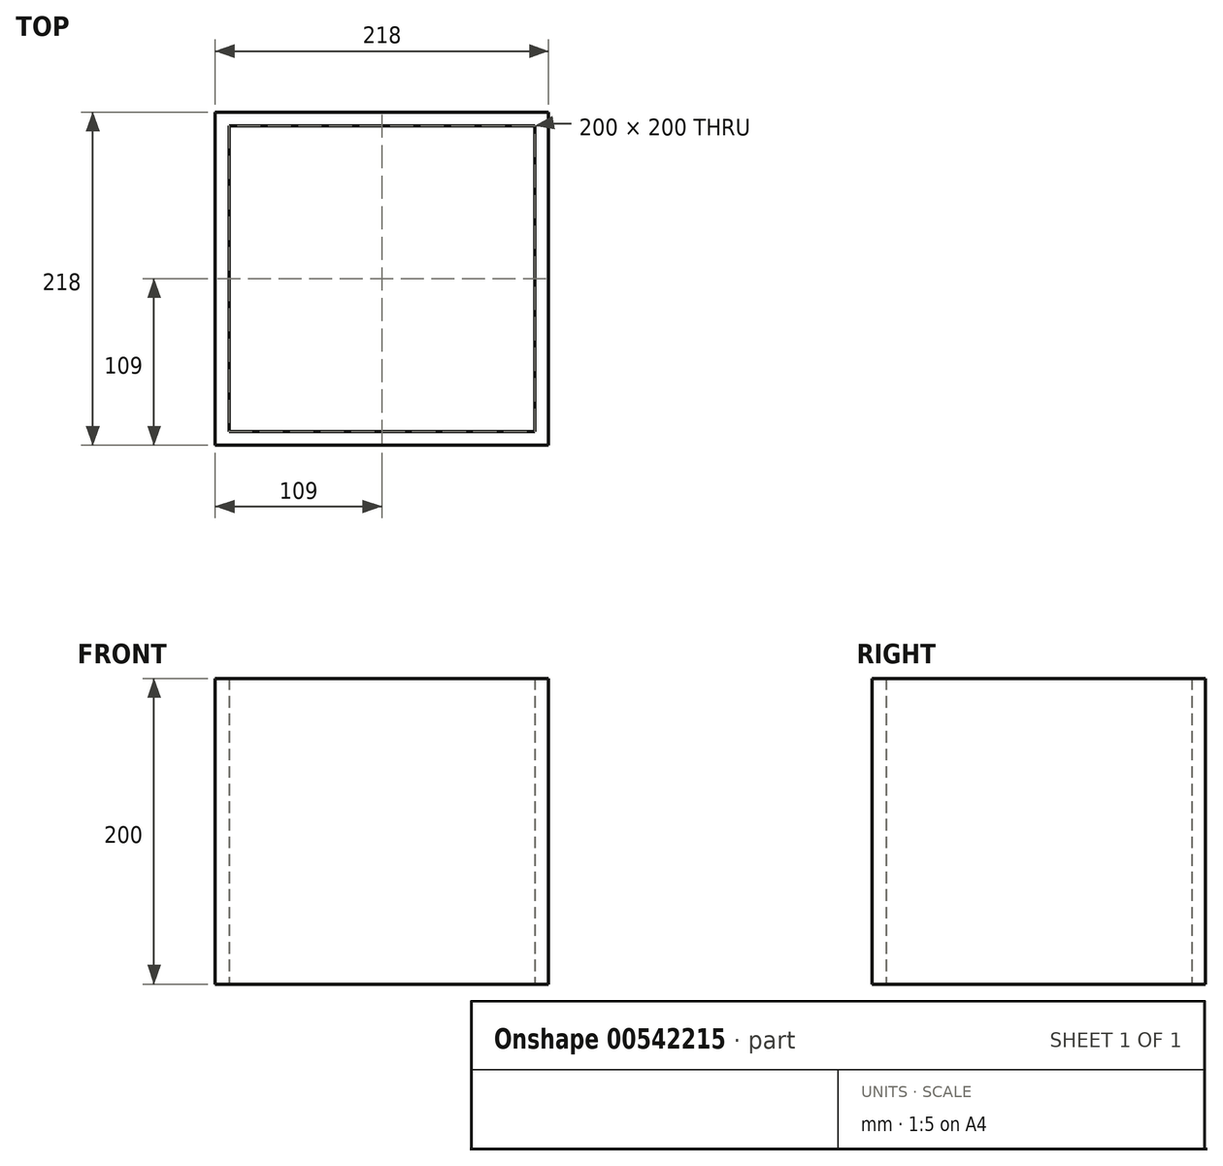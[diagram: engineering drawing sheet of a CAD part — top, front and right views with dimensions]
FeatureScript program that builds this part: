
annotation { "Feature Type Name" : "Feature", "Feature Type Description" : "" }
export const myFeature = defineFeature(function(context is Context, id is Id, definition is map)
    precondition{}
    {
        {
            var Q0;
            Q0=qCreatedBy(makeId("Top.planeOp"),FACE);
            var sketch = newSketch(context, id + "F0", { "sketchPlane" : qUnion([Q0])});
            skLineSegment(sketch, "E0.bottom", {"start": v(109, -109) * mm, "end": v(-109, -109) * mm});
            skLineSegment(sketch, "E0.top", {"start": v(109, 109) * mm, "end": v(-109, 109) * mm});
            skLineSegment(sketch, "E0.left", {"start": v(109, -109) * mm, "end": v(109, 109) * mm});
            skLineSegment(sketch, "E0.right", {"start": v(-109, -109) * mm, "end": v(-109, 109) * mm});
            skPoint(sketch, "E0.middle", {"position": v(0, 0) * mm});
            skLineSegment(sketch, "E1.bottom", {"start": v(-100, -100) * mm, "end": v(100, -100) * mm});
            skLineSegment(sketch, "E1.top", {"start": v(-100, 100) * mm, "end": v(100, 100) * mm});
            skLineSegment(sketch, "E1.left", {"start": v(-100, -100) * mm, "end": v(-100, 100) * mm});
            skLineSegment(sketch, "E1.right", {"start": v(100, -100) * mm, "end": v(100, 100) * mm});
            skLineSegment(sketch, "E2", {"start": v(-109, 100) * mm, "end": v(-100, 100) * mm});
            skLineSegment(sketch, "E3", {"start": v(-100, -109) * mm, "end": v(-100, -100) * mm});
            skLineSegment(sketch, "E4", {"start": v(109, -100) * mm, "end": v(100, -100) * mm});
            skLineSegment(sketch, "E5", {"start": v(100, 100) * mm, "end": v(100, 109) * mm});
            skSolve(sketch);
        }
        {
            var Q0;
            Q0 = qSketchRegion(id + "F0", true);
            extrude(context, id + "F1", {"entities" : qUnion([Q0]), "depth" : 200 * mm, "offsetDistance" : 25.4 * mm});
        }
    });
